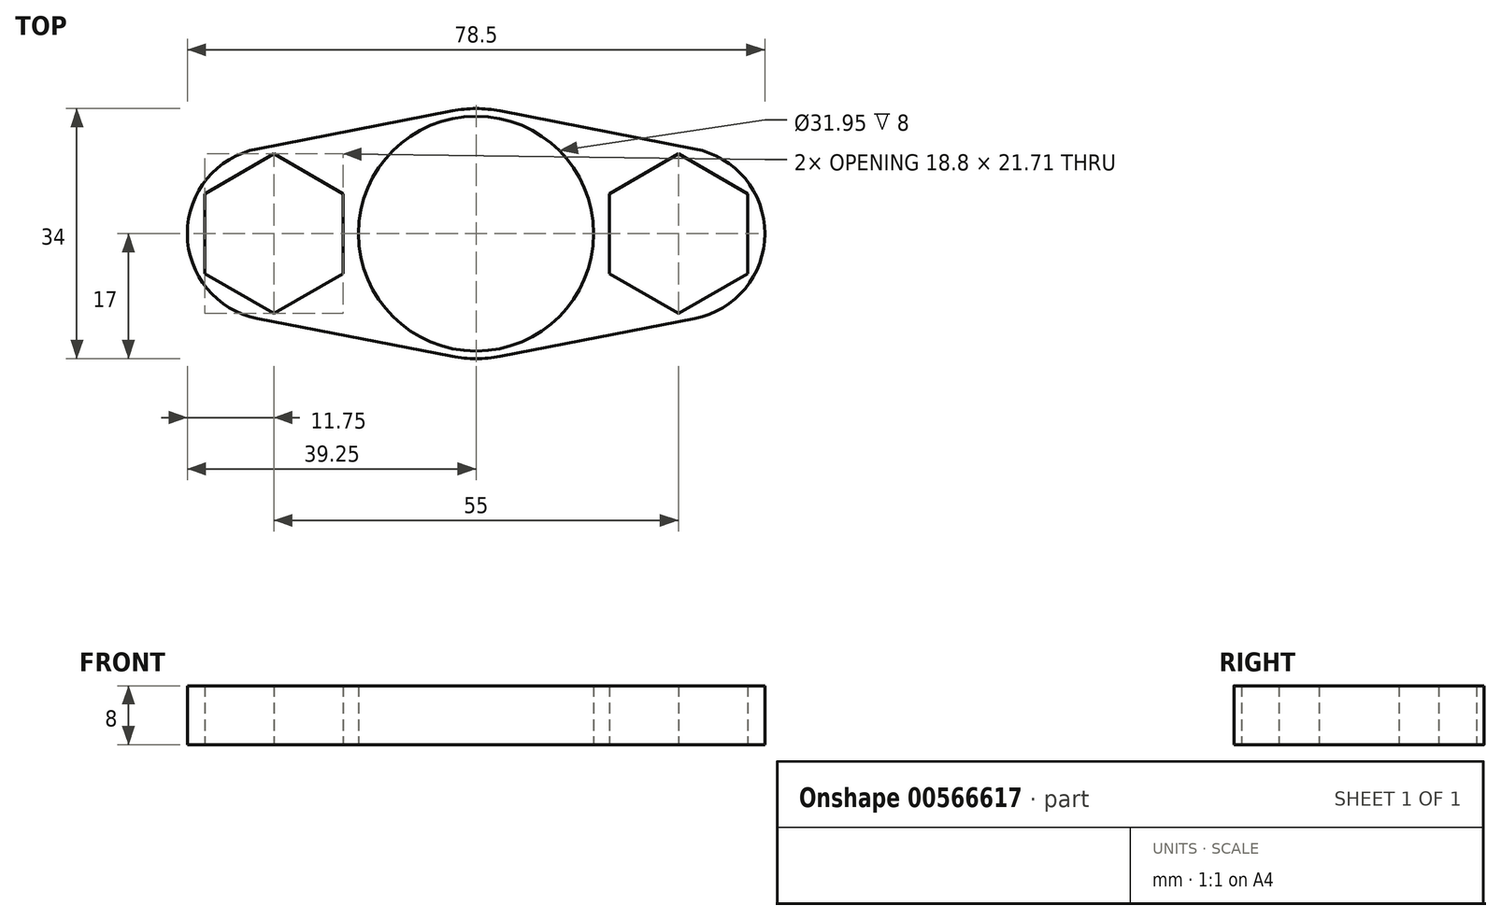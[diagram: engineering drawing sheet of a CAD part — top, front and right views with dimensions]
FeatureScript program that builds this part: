
annotation { "Feature Type Name" : "Feature", "Feature Type Description" : "" }
export const myFeature = defineFeature(function(context is Context, id is Id, definition is map)
    precondition{}
    {
        {
            var Q0;
            Q0=qCreatedBy(makeId("Top.planeOp"),FACE);
            var sketch = newSketch(context, id + "F0", { "sketchPlane" : qUnion([Q0])});
            skArc(sketch, "E0", {"start": v(-29.74, 11.53) * mm, "mid": v(-39.25, 0) * mm, "end": v(-29.74, -11.53) * mm});
            skCircle(sketch, "E1.cCircle", {"center": v(-27.5, 0) * mm, "radius": 9.4 * mm, "construction": true});
            skLineSegment(sketch, "E1.0", {"start": v(-36.9, -5.43) * mm, "end": v(-36.9, 5.43) * mm});
            skLineSegment(sketch, "E1.1", {"start": v(-36.9, 5.43) * mm, "end": v(-27.5, 10.85) * mm});
            skLineSegment(sketch, "E1.2", {"start": v(-27.5, 10.85) * mm, "end": v(-18.1, 5.43) * mm});
            skLineSegment(sketch, "E1.3", {"start": v(-18.1, 5.43) * mm, "end": v(-18.1, -5.43) * mm});
            skLineSegment(sketch, "E1.4", {"start": v(-18.1, -5.43) * mm, "end": v(-27.5, -10.85) * mm});
            skLineSegment(sketch, "E1.5", {"start": v(-27.5, -10.85) * mm, "end": v(-36.9, -5.43) * mm});
            skPoint(sketch, "E1.0.midPoint", {"position": v(-36.9, 0) * mm});
            skLineSegment(sketch, "E2", {"start": v(-3.25, 16.69) * mm, "end": v(-29.74, 11.53) * mm});
            skLineSegment(sketch, "E3.MirrorCS", {"start": v(-3.25, -16.69) * mm, "end": v(-29.74, -11.53) * mm});
            skArc(sketch, "E4.trimOffspring", {"start": v(-3.25, -16.69) * mm, "mid": v(-1.63, -16.92) * mm, "end": v(0, -17) * mm});
            skArc(sketch, "E5", {"start": v(0, 17) * mm, "mid": v(-1.63, 16.92) * mm, "end": v(-3.25, 16.69) * mm});
            skArc(sketch, "E6", {"start": v(0, 15.97) * mm, "mid": v(-15.97, 0) * mm, "end": v(0, -15.97) * mm});
            skArc(sketch, "E7.MirrorCS", {"start": v(0, 17) * mm, "mid": v(1.63, 16.92) * mm, "end": v(3.25, 16.69) * mm});
            skArc(sketch, "E8.MirrorCS", {"start": v(0, 15.97) * mm, "mid": v(15.97, 0) * mm, "end": v(0, -15.97) * mm});
            skArc(sketch, "E9.MirrorCS", {"start": v(3.25, -16.69) * mm, "mid": v(1.63, -16.92) * mm, "end": v(0, -17) * mm});
            skLineSegment(sketch, "E10.MirrorCS", {"start": v(3.25, -16.69) * mm, "end": v(29.74, -11.53) * mm});
            skArc(sketch, "E11.MirrorCS", {"start": v(29.74, 11.53) * mm, "mid": v(39.25, 0) * mm, "end": v(29.74, -11.53) * mm});
            skLineSegment(sketch, "E12.MirrorCS", {"start": v(3.25, 16.69) * mm, "end": v(29.74, 11.53) * mm});
            skCircle(sketch, "E13.MirrorC", {"center": v(27.5, 0) * mm, "radius": 9.4 * mm, "construction": true});
            skLineSegment(sketch, "E14.MirrorCS", {"start": v(36.9, 5.43) * mm, "end": v(27.5, 10.85) * mm});
            skLineSegment(sketch, "E15.MirrorCS", {"start": v(27.5, 10.85) * mm, "end": v(18.1, 5.43) * mm});
            skLineSegment(sketch, "E16.MirrorCS", {"start": v(18.1, 5.43) * mm, "end": v(18.1, -5.43) * mm});
            skLineSegment(sketch, "E17.MirrorCS", {"start": v(18.1, -5.43) * mm, "end": v(27.5, -10.85) * mm});
            skLineSegment(sketch, "E18.MirrorCS", {"start": v(27.5, -10.85) * mm, "end": v(36.9, -5.43) * mm});
            skLineSegment(sketch, "E19.MirrorCS", {"start": v(36.9, -5.43) * mm, "end": v(36.9, 5.43) * mm});
            skSolve(sketch);
        }
        {
            var Q0;
            Q0=makeQuery(id+"F0.imprint","IMPRINT",FACE,{"disambiguationData":[TD([[makeQuery(id+"F0.imprint","IMPRINT",EDGE,{"derivedFrom":sQuery(id+"F0.wireOp",EDGE,"E0")}),1.0]])]});
            extrude(context, id + "F1", {"entities" : qUnion([Q0]), "endBound" : BoundingType.SYMMETRIC, "depth" : 8 * mm, "offsetDistance" : 25 * mm});
        }
    });
